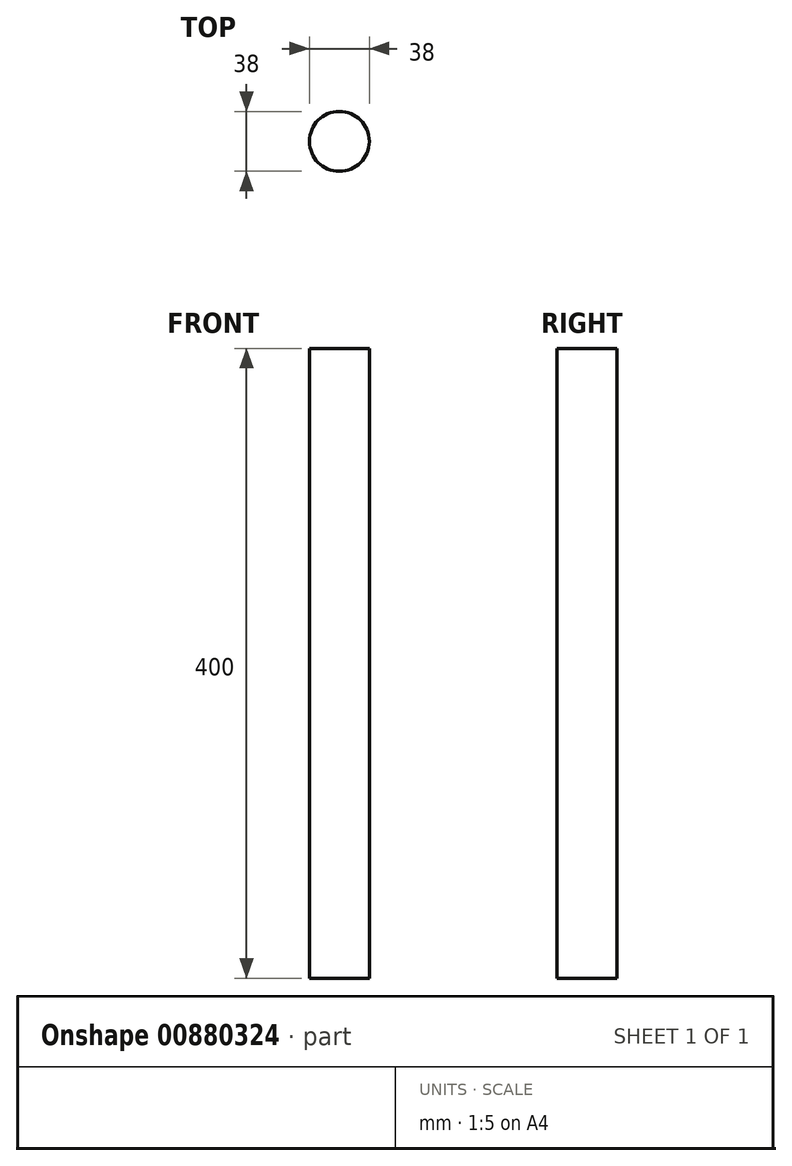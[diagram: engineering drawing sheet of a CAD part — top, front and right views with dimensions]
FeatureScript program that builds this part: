
annotation { "Feature Type Name" : "Feature", "Feature Type Description" : "" }
export const myFeature = defineFeature(function(context is Context, id is Id, definition is map)
    precondition{}
    {
        {
            var Q0;
            Q0=qCreatedBy(makeId("Top.planeOp"),FACE);
            var sketch = newSketch(context, id + "F0", { "sketchPlane" : qUnion([Q0])});
            skCircle(sketch, "E0", {"center": v(0, 0) * mm, "radius": 19 * mm});
            skSolve(sketch);
        }
        {
            var Q0;
            Q0=makeQuery(id+"F0.imprint","IMPRINT",FACE,{"disambiguationData":[TD([[makeQuery(id+"F0.imprint","IMPRINT",EDGE,{"derivedFrom":sQuery(id+"F0.wireOp",EDGE,"E0")}),1.0]])]});
            extrude(context, id + "F1", {"entities" : qUnion([Q0]), "depth" : 400 * mm, "offsetDistance" : 25 * mm});
        }
    });
